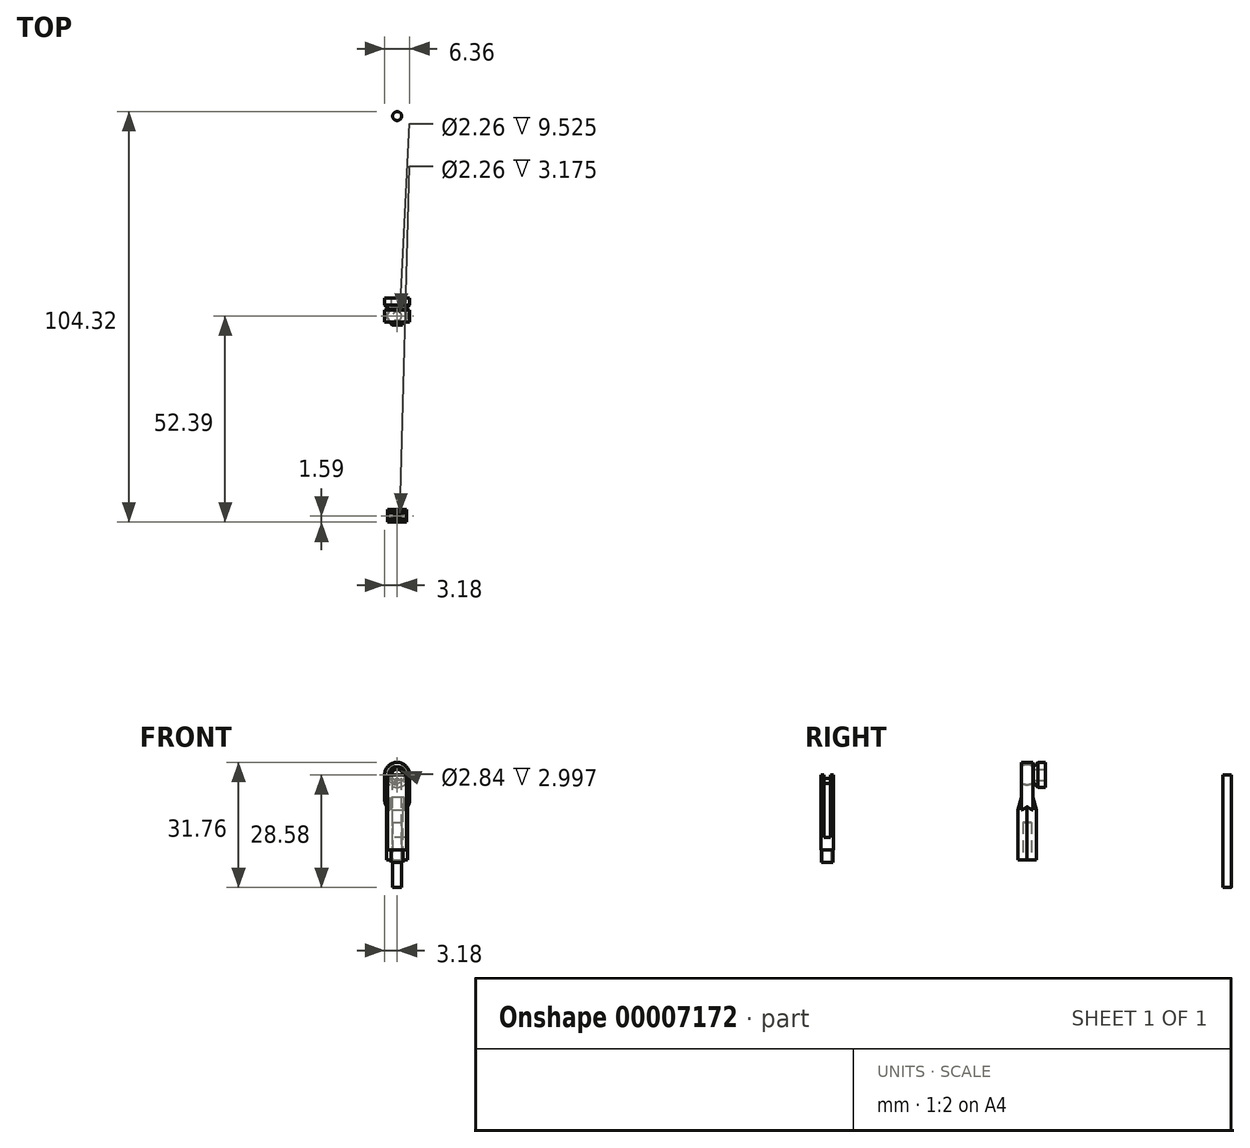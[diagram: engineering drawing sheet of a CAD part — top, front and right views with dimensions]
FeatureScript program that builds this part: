
annotation { "Feature Type Name" : "Feature", "Feature Type Description" : "" }
export const myFeature = defineFeature(function(context is Context, id is Id, definition is map)
    precondition{}
    {
        {
            var Q0;
            Q0=qCreatedBy(makeId("Right.planeOp"),FACE);
            var sketch = newSketch(context, id + "F0", { "sketchPlane" : qUnion([Q0])});
            skLineSegment(sketch, "E0", {"start": v(-1.59, 0) * mm, "end": v(1.59, 0) * mm, "construction": true});
            skLineSegment(sketch, "E1", {"start": v(-1.59, 1.42) * mm, "end": v(1.59, 1.42) * mm});
            skLineSegment(sketch, "E2", {"start": v(1.59, 1.42) * mm, "end": v(1.59, 1.98) * mm});
            skLineSegment(sketch, "E3", {"start": v(-1.59, 1.42) * mm, "end": v(-1.59, 1.98) * mm});
            skArc(sketch, "E4", {"start": v(1.59, 1.98) * mm, "mid": v(0, 2.54) * mm, "end": v(-1.59, 1.98) * mm});
            skLineSegment(sketch, "E5", {"start": v(-1.59, 1.42) * mm, "end": v(-1.59, 0) * mm});
            skLineSegment(sketch, "E6", {"start": v(1.59, 1.42) * mm, "end": v(1.59, 0) * mm});
            skLineSegment(sketch, "E7", {"start": v(1.59, 0) * mm, "end": v(-1.59, 0) * mm});
            skSolve(sketch);
        }
        {
            var Q0;
            Q0=makeQuery(id+"F0.imprint","IMPRINT",FACE,{"disambiguationData":[TD([[makeQuery(id+"F0.imprint","IMPRINT",EDGE,{"derivedFrom":sQuery(id+"F0.wireOp",EDGE,"E1")}),1.0]])]});
            var Q1;
            Q1=sQuery(id+"F0.wireOp",EDGE,"E0");
            revolve(context, id + "F1", {"entities" : qUnion([Q0]), "axis" : qUnion([Q1]), "revolveType" : RevolveType.FULL});
        }
        {
            var Q0;
            Q0=qCreatedBy(makeId("Front.planeOp"),FACE);
            var sketch = newSketch(context, id + "F2", { "sketchPlane" : qUnion([Q0])});
            skArc(sketch, "E8", {"start": v(3.18, 0) * mm, "mid": v(0, 3.18) * mm, "end": v(-3.18, 0) * mm});
            skLineSegment(sketch, "E9", {"start": v(-3.18, 0) * mm, "end": v(-3.18, -6.35) * mm});
            skLineSegment(sketch, "E10", {"start": v(-3.17, -6.35) * mm, "end": v(3.17, -6.35) * mm, "construction": true});
            skLineSegment(sketch, "E11", {"start": v(3.18, -6.35) * mm, "end": v(3.17, 0) * mm});
            skArc(sketch, "E12", {"start": v(-3.17, -6.35) * mm, "mid": v(0, -9.52) * mm, "end": v(3.17, -6.35) * mm});
            skSolve(sketch);
        }
        {
            var Q0;
            Q0 = qSketchRegion(id + "F2", true);
            extrude(context, id + "F3", {"entities" : qUnion([Q0]), "endBound" : BoundingType.SYMMETRIC, "depth" : 3 * mm});
        }
        {
            var Q0;
            Q0=makeQuery(id+"F0.imprint","IMPRINT",FACE,{"disambiguationData":[TD([[makeQuery(id+"F0.imprint","IMPRINT",EDGE,{"derivedFrom":sQuery(id+"F0.wireOp",EDGE,"E1")}),-1.0]])]});
            var Q1;
            Q1=makeQuery(id+"F0.imprint","IMPRINT",FACE,{"disambiguationData":[TD([[makeQuery(id+"F0.imprint","IMPRINT",EDGE,{"derivedFrom":sQuery(id+"F0.wireOp",EDGE,"E1")}),1.0]])]});
            var Q2;
            Q2=sQuery(id+"F0.wireOp",EDGE,"E7");
            revolve(context, id + "F4", {"operationType" : NewBodyOperationType.REMOVE, "entities" : qUnion([Q0, Q1]), "axis" : qUnion([Q2]), "revolveType" : RevolveType.FULL, "oppositeDirection" : true});
        }
        {
            var Q0;
            Q0=qCreatedBy(makeId("Top.planeOp"),FACE);
            cPlane(context, id + "F5", {"entities" : qUnion([Q0]), "cplaneType" : CPlaneType.OFFSET, "offset" : 21.59 * mm, "oppositeDirection" : true, "width" : 152.4 * mm, "height" : 152.4 * mm});
        }
        {
            var Q0;
            Q0=qCreatedBy(id+"F5.planeOp",FACE);
            var sketch = newSketch(context, id + "F6", { "sketchPlane" : qUnion([Q0])});
            skCircle(sketch, "E13.cCircle", {"center": v(0, 0) * mm, "radius": 2.67 * mm, "construction": true});
            skLineSegment(sketch, "E13.0", {"start": v(2.67, 0) * mm, "end": v(1.33, -2.3) * mm});
            skLineSegment(sketch, "E13.1", {"start": v(1.33, -2.3) * mm, "end": v(-1.33, -2.3) * mm});
            skLineSegment(sketch, "E13.2", {"start": v(-1.33, -2.3) * mm, "end": v(-2.67, 0) * mm});
            skLineSegment(sketch, "E13.3", {"start": v(-2.67, 0) * mm, "end": v(-1.33, 2.3) * mm});
            skLineSegment(sketch, "E13.4", {"start": v(-1.33, 2.3) * mm, "end": v(1.33, 2.3) * mm});
            skLineSegment(sketch, "E13.5", {"start": v(1.33, 2.3) * mm, "end": v(2.67, 0) * mm});
            skSolve(sketch);
        }
        {
            var Q0;
            Q0 = qSketchRegion(id + "F6", true);
            extrude(context, id + "F7", {"entities" : qUnion([Q0]), "operationType" : NewBodyOperationType.ADD, "depth" : 15.88 * mm});
        }
        {
            var Q0;
            Q0=qCreatedBy(makeId("Right.planeOp"),FACE);
            var sketch = newSketch(context, id + "F8", { "sketchPlane" : qUnion([Q0])});
            skLineSegment(sketch, "E14.0", {"start": v(1.5, -6.35) * mm, "end": v(1.5, 0) * mm});
            skLineSegment(sketch, "E15.0", {"start": v(-1.5, -6.35) * mm, "end": v(-1.5, 0) * mm});
            skLineSegment(sketch, "E16.0", {"start": v(1.5, -8.96) * mm, "end": v(1.5, -6.35) * mm});
            skLineSegment(sketch, "E17.0", {"start": v(-1.5, -8.96) * mm, "end": v(-1.5, -6.35) * mm});
            skLineSegment(sketch, "E18.0", {"start": v(-2.3, -5.72) * mm, "end": v(-2.3, -21.59) * mm});
            skLineSegment(sketch, "E19.0", {"start": v(2.3, -5.72) * mm, "end": v(2.3, -21.59) * mm});
            skLineSegment(sketch, "E20", {"start": v(1.5, -8.96) * mm, "end": v(2.3, -8.96) * mm});
            skLineSegment(sketch, "E21", {"start": v(2.3, -8.96) * mm, "end": v(1.5, -5.72) * mm});
            skLineSegment(sketch, "E22", {"start": v(-1.5, -5.72) * mm, "end": v(-2.3, -8.96) * mm});
            skLineSegment(sketch, "E23", {"start": v(-2.3, -8.96) * mm, "end": v(-1.5, -8.96) * mm});
            skLineSegment(sketch, "E24.0", {"start": v(2.3, -5.72) * mm, "end": v(1.5, -5.72) * mm});
            skLineSegment(sketch, "E25.0", {"start": v(-1.5, -5.72) * mm, "end": v(-2.3, -5.72) * mm});
            skSolve(sketch);
        }
        {
            var Q0;
            {var subQ1=sQuery(id+"F8.wireOp",EDGE,"E21");Q0=makeQuery(id+"F8.imprint","IMPRINT",FACE,{"disambiguationData":[TD([[makeQuery(id+"F8.imprint","IMPRINT",EDGE,{"derivedFrom":subQ1}),-1.0]])]});}
            var Q1;
            {var subQ1=sQuery(id+"F8.wireOp",EDGE,"E22");Q1=makeQuery(id+"F8.imprint","IMPRINT",FACE,{"disambiguationData":[TD([[makeQuery(id+"F8.imprint","IMPRINT",EDGE,{"derivedFrom":subQ1}),-1.0]])]});}
            extrude(context, id + "F9", {"entities" : qUnion([Q0, Q1]), "operationType" : NewBodyOperationType.REMOVE, "endBound" : BoundingType.SYMMETRIC, "oppositeDirection" : true, "depth" : 25.4 * mm});
        }
        {
            var Q0;
            Q0=makeQuery(id+"F7.opExtrude","CAP_FACE",FACE,{"disambiguationData":[OSD([sQuery(id+"F6.wireOp",EDGE,"E13.0"),sQuery(id+"F6.wireOp",EDGE,"E13.1"),sQuery(id+"F6.wireOp",EDGE,"E13.2"),sQuery(id+"F6.wireOp",EDGE,"E13.3"),sQuery(id+"F6.wireOp",EDGE,"E13.4"),sQuery(id+"F6.wireOp",EDGE,"E13.5")])],"isStart":true});
            var sketch = newSketch(context, id + "F10", { "sketchPlane" : qUnion([Q0])});
            skCircle(sketch, "E26", {"center": v(0, 0) * mm, "radius": 1.13 * mm});
            skSolve(sketch);
        }
        {
            var Q0;
            Q0=makeQuery(id+"F10.imprint","IMPRINT",FACE,{"disambiguationData":[TD([[makeQuery(id+"F10.imprint","IMPRINT",EDGE,{"derivedFrom":sQuery(id+"F10.wireOp",EDGE,"E26")}),1.0]])]});
            extrude(context, id + "F11", {"entities" : qUnion([Q0]), "operationType" : NewBodyOperationType.REMOVE, "oppositeDirection" : true, "depth" : 9.52 * mm});
        }
        {
            var Q0;
            Q0=qCreatedBy(makeId("Right.planeOp"),FACE);
            var sketch = newSketch(context, id + "F12", { "sketchPlane" : qUnion([Q0])});
            skLineSegment(sketch, "E27.0", {"start": v(1.59, -1.98) * mm, "end": v(1.59, 1.98) * mm});
            skPoint(sketch, "E28", {"position": v(1.59, 0) * mm});
            skLineSegment(sketch, "E29", {"start": v(1.59, -1.98) * mm, "end": v(2.78, -3.18) * mm});
            skLineSegment(sketch, "E30", {"start": v(2.78, -3.17) * mm, "end": v(4.58, -3.17) * mm});
            skLineSegment(sketch, "E31", {"start": v(4.58, -3.18) * mm, "end": v(4.58, -1.42) * mm});
            skLineSegment(sketch, "E32", {"start": v(4.58, -1.42) * mm, "end": v(1.59, -1.42) * mm});
            skLineSegment(sketch, "E33", {"start": v(1.59, -1.42) * mm, "end": v(1.59, -1.98) * mm});
            skSolve(sketch);
        }
        {
            var Q0;
            Q0=makeQuery(id+"F12.imprint","IMPRINT",FACE,{"disambiguationData":[TD([[makeQuery(id+"F12.imprint","IMPRINT",EDGE,{"derivedFrom":sQuery(id+"F12.wireOp",EDGE,"E29")}),1.0]])]});
            var Q1;
            Q1=sQuery(id+"F0.wireOp",EDGE,"E7");
            revolve(context, id + "F13", {"entities" : qUnion([Q0]), "axis" : qUnion([Q1]), "revolveType" : RevolveType.FULL});
        }
        {
            var Q0;
            Q0=qCreatedBy(makeId("Front.planeOp"),FACE);
            cPlane(context, id + "F14", {"entities" : qUnion([Q0]), "cplaneType" : CPlaneType.OFFSET, "offset" : 50.8 * mm, "width" : 152.4 * mm, "height" : 152.4 * mm});
        }
        {
            var Q0;
            Q0=qCreatedBy(makeId("Right.planeOp"),FACE);
            var sketch = newSketch(context, id + "F15", { "sketchPlane" : qUnion([Q0])});
            skLineSegment(sketch, "E34.bottom", {"start": v(-51.6, 0) * mm, "end": v(-50, 0) * mm});
            skLineSegment(sketch, "E34.top", {"start": v(-51.6, -15.88) * mm, "end": v(-50, -15.88) * mm});
            skLineSegment(sketch, "E34.left", {"start": v(-51.6, 0) * mm, "end": v(-51.6, -15.88) * mm});
            skLineSegment(sketch, "E34.right", {"start": v(-50, 0) * mm, "end": v(-50, -15.88) * mm});
            skLineSegment(sketch, "E35.bottom", {"start": v(-52.39, 0) * mm, "end": v(-51.6, 0) * mm});
            skLineSegment(sketch, "E35.top", {"start": v(-52.39, -19.05) * mm, "end": v(-49.21, -19.05) * mm});
            skLineSegment(sketch, "E35.left", {"start": v(-52.39, 0) * mm, "end": v(-52.39, -19.05) * mm});
            skLineSegment(sketch, "E35.right", {"start": v(-49.21, 0) * mm, "end": v(-49.21, -19.05) * mm});
            skLineSegment(sketch, "E36", {"start": v(-50, 0) * mm, "end": v(-49.21, 0) * mm});
            skPoint(sketch, "E37", {"position": v(-50.8, 0) * mm});
            skSolve(sketch);
        }
        {
            var Q0;
            Q0=makeQuery(id+"F15.imprint","IMPRINT",FACE,{"disambiguationData":[TD([[makeQuery(id+"F15.imprint","IMPRINT",EDGE,{"derivedFrom":sQuery(id+"F15.wireOp",EDGE,"E34.top")}),-1.0]])]});
            extrude(context, id + "F16", {"entities" : qUnion([Q0]), "endBound" : BoundingType.SYMMETRIC, "depth" : 4.76 * mm});
        }
        {
            var Q0;
            Q0=makeQuery(id+"F16.opExtrude","SWEPT_FACE",FACE,{"disambiguationData":[OSD([sQuery(id+"F15.wireOp",EDGE,"E35.right")])]});
            var sketch = newSketch(context, id + "F17", { "sketchPlane" : qUnion([Q0])});
            skCircle(sketch, "E38", {"center": v(0, -1.59) * mm, "radius": 0.64 * mm});
            skSolve(sketch);
        }
        {
            var Q0;
            Q0=makeQuery(id+"F17.imprint","IMPRINT",FACE,{"disambiguationData":[TD([[makeQuery(id+"F17.imprint","IMPRINT",EDGE,{"derivedFrom":sQuery(id+"F17.wireOp",EDGE,"E38")}),1.0]])]});
            var Q1;
            Q1=makeQuery(id+"F16.opExtrude","SWEPT_FACE",FACE,{"disambiguationData":[OSD([sQuery(id+"F15.wireOp",EDGE,"E35.left")])]});
            extrude(context, id + "F18", {"entities" : qUnion([Q0]), "operationType" : NewBodyOperationType.ADD, "endBound" : BoundingType.UP_TO_SURFACE, "oppositeDirection" : true, "endBoundEntityFace" : qUnion([Q1]), "depth" : 25.4 * mm});
        }
        {
            var Q0;
            Q0=makeQuery(id+"F16.opExtrude","SWEPT_FACE",FACE,{"disambiguationData":[OSD([sQuery(id+"F15.wireOp",EDGE,"E35.top")])]});
            var sketch = newSketch(context, id + "F19", { "sketchPlane" : qUnion([Q0])});
            skCircle(sketch, "E39", {"center": v(0, 50.8) * mm, "radius": 1.5 * mm});
            skPoint(sketch, "E40", {"position": v(0, 49.21) * mm});
            skPoint(sketch, "E41", {"position": v(2.38, 50.8) * mm});
            skCircle(sketch, "E42", {"center": v(0, 50.8) * mm, "radius": 1.13 * mm});
            skSolve(sketch);
        }
        {
            var Q0;
            Q0=makeQuery(id+"F19.imprint","IMPRINT",FACE,{"disambiguationData":[TD([[makeQuery(id+"F19.imprint","IMPRINT",EDGE,{"derivedFrom":sQuery(id+"F19.wireOp",EDGE,"E39")}),1.0]])]});
            extrude(context, id + "F20", {"entities" : qUnion([Q0]), "operationType" : NewBodyOperationType.ADD, "depth" : 3.17 * mm});
        }
        {
            var Q0;
            Q0=qCreatedBy(makeId("Top.planeOp"),FACE);
            var sketch = newSketch(context, id + "F21", { "sketchPlane" : qUnion([Q0])});
            skCircle(sketch, "E43", {"center": v(0, 50.8) * mm, "radius": 1.13 * mm});
            skSolve(sketch);
        }
        {
            var Q0;
            Q0 = qSketchRegion(id + "F21", true);
            extrude(context, id + "F22", {"entities" : qUnion([Q0]), "oppositeDirection" : true, "depth" : 28.57 * mm});
        }
    });
